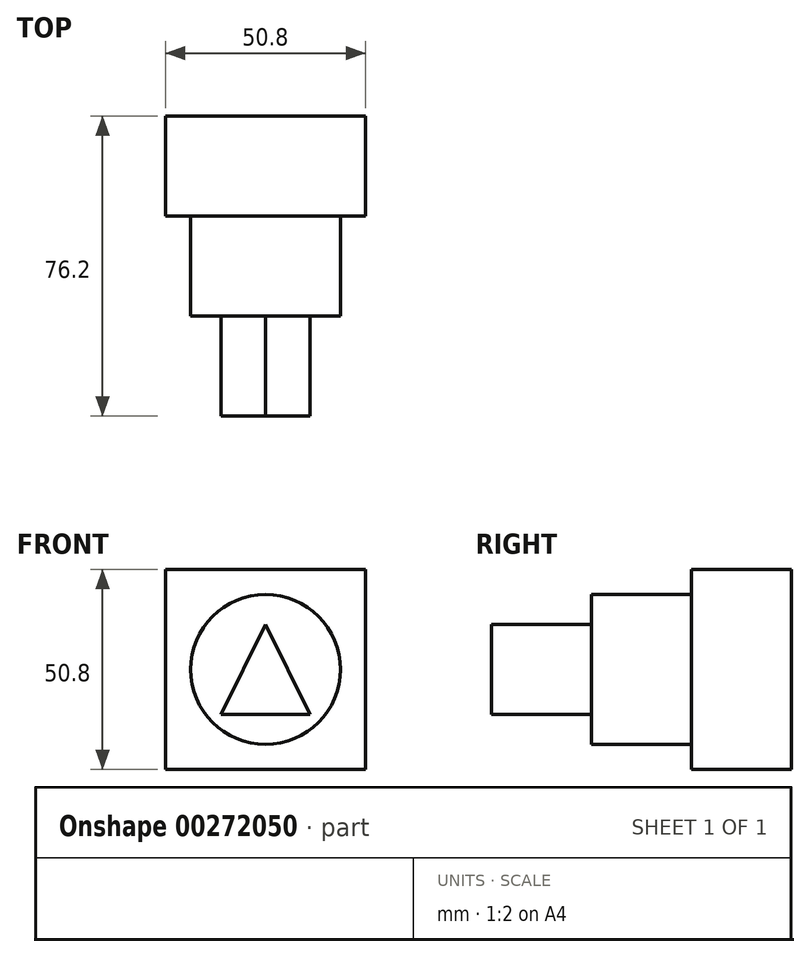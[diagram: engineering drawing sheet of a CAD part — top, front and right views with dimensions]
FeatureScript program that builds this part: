
annotation { "Feature Type Name" : "Feature", "Feature Type Description" : "" }
export const myFeature = defineFeature(function(context is Context, id is Id, definition is map)
    precondition{}
    {
        {
            var Q0;
            Q0=qCreatedBy(makeId("Front.planeOp"),FACE);
            var sketch = newSketch(context, id + "F0", { "sketchPlane" : qUnion([Q0])});
            skLineSegment(sketch, "E0.bottom", {"start": v(25.4, -25.4) * mm, "end": v(-25.4, -25.4) * mm});
            skLineSegment(sketch, "E0.top", {"start": v(25.4, 25.4) * mm, "end": v(-25.4, 25.4) * mm});
            skLineSegment(sketch, "E0.left", {"start": v(25.4, -25.4) * mm, "end": v(25.4, 25.4) * mm});
            skLineSegment(sketch, "E0.right", {"start": v(-25.4, -25.4) * mm, "end": v(-25.4, 25.4) * mm});
            skPoint(sketch, "E0.middle", {"position": v(0, 0) * mm});
            skSolve(sketch);
        }
        {
            var Q0;
            Q0 = qSketchRegion(id + "F0", true);
            extrude(context, id + "F1", {"entities" : qUnion([Q0]), "depth" : 25.4 * mm});
        }
        {
            var Q0;
            Q0=makeQuery(id+"F1.opExtrude","CAP_FACE",FACE,{"disambiguationData":[OSD([sQuery(id+"F0.wireOp",EDGE,"E0.bottom"),sQuery(id+"F0.wireOp",EDGE,"E0.top"),sQuery(id+"F0.wireOp",EDGE,"E0.left"),sQuery(id+"F0.wireOp",EDGE,"E0.right")])],"isStart":false});
            var sketch = newSketch(context, id + "F2", { "sketchPlane" : qUnion([Q0])});
            skCircle(sketch, "E1", {"center": v(0, 0) * mm, "radius": 19.05 * mm});
            skSolve(sketch);
        }
        {
            var Q0;
            Q0 = qSketchRegion(id + "F2", true);
            extrude(context, id + "F3", {"entities" : qUnion([Q0]), "operationType" : NewBodyOperationType.ADD, "depth" : 25.4 * mm});
        }
        {
            var Q0;
            Q0=makeQuery(id+"F3.opExtrude","CAP_FACE",FACE,{"disambiguationData":[OSD([sQuery(id+"F2.wireOp",EDGE,"E1")])],"isStart":false});
            var sketch = newSketch(context, id + "F4", { "sketchPlane" : qUnion([Q0])});
            skLineSegment(sketch, "E2", {"start": v(0, 11.43) * mm, "end": v(-11.34, -11.43) * mm});
            skLineSegment(sketch, "E3", {"start": v(-11.34, -11.43) * mm, "end": v(11.34, -11.43) * mm});
            skLineSegment(sketch, "E4", {"start": v(11.34, -11.43) * mm, "end": v(0, 11.43) * mm});
            skSolve(sketch);
        }
        {
            var Q0;
            Q0 = qSketchRegion(id + "F4", true);
            extrude(context, id + "F5", {"entities" : qUnion([Q0]), "operationType" : NewBodyOperationType.ADD, "depth" : 25.4 * mm});
        }
    });
